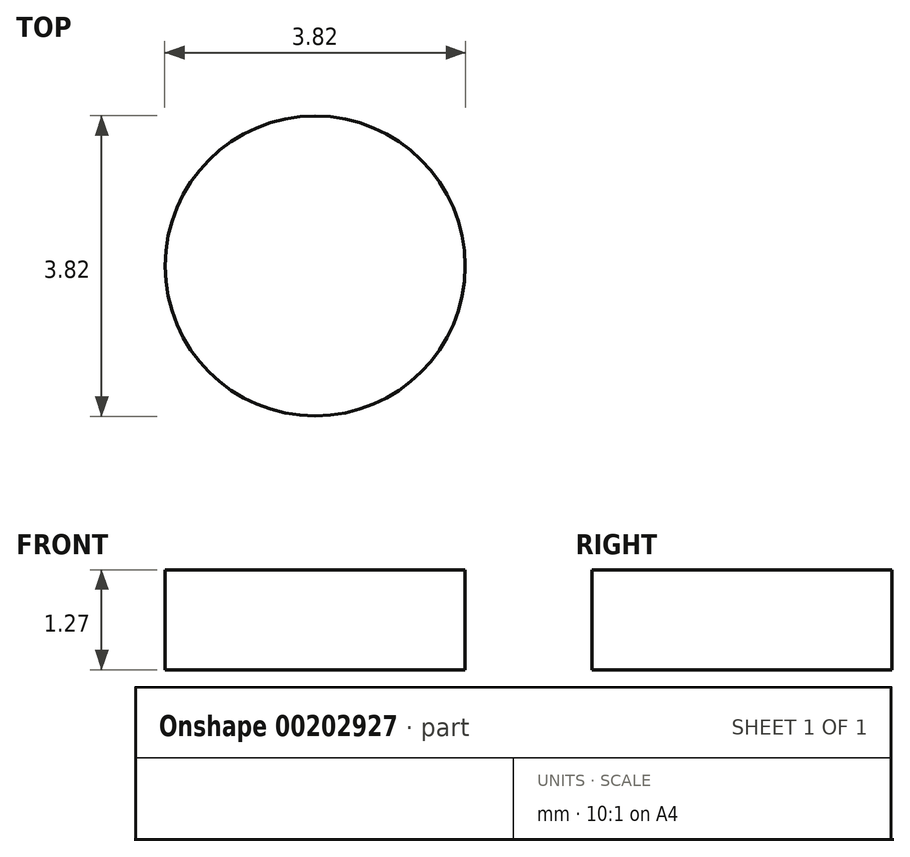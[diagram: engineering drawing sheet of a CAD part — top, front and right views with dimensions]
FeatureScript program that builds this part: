
annotation { "Feature Type Name" : "Feature", "Feature Type Description" : "" }
export const myFeature = defineFeature(function(context is Context, id is Id, definition is map)
    precondition{}
    {
        {
            var Q0;
            Q0=qCreatedBy(makeId("Top.planeOp"),FACE);
            var sketch = newSketch(context, id + "F0", { "sketchPlane" : qUnion([Q0])});
            skCircle(sketch, "E0", {"center": v(0, 0) * mm, "radius": 1.9 * mm});
            skSolve(sketch);
        }
        {
            var Q0;
            Q0 = qSketchRegion(id + "F0", true);
            extrude(context, id + "F1", {"entities" : qUnion([Q0]), "depth" : 1.27 * mm});
        }
    });
